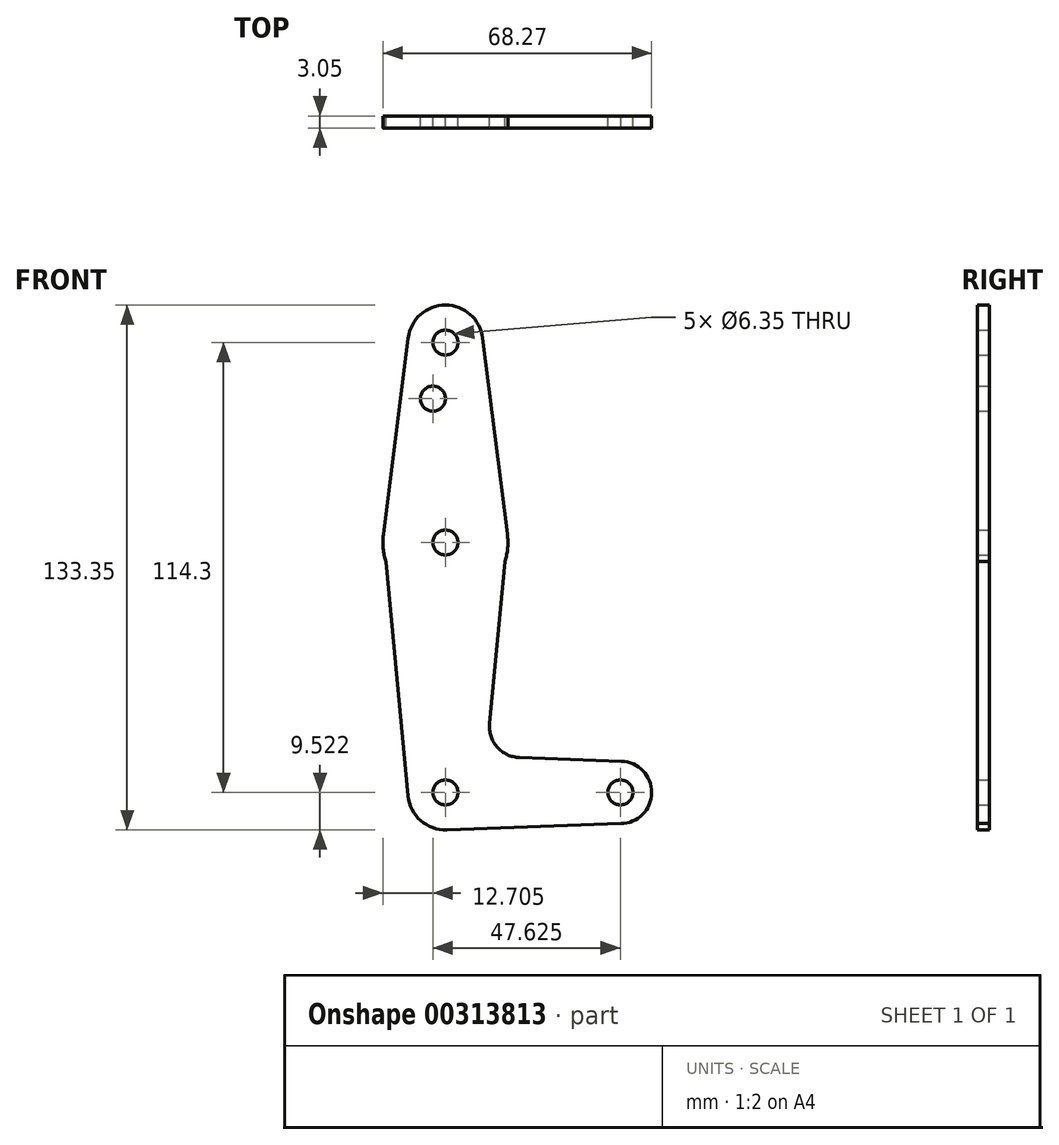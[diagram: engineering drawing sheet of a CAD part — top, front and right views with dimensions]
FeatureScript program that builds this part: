
annotation { "Feature Type Name" : "Feature", "Feature Type Description" : "" }
export const myFeature = defineFeature(function(context is Context, id is Id, definition is map)
    precondition{}
    {
        {
            var Q0;
            Q0=qCreatedBy(makeId("Front.planeOp"),FACE);
            var sketch = newSketch(context, id + "F0", { "sketchPlane" : qUnion([Q0])});
            skCircle(sketch, "E0", {"center": v(0, 72.35) * mm, "radius": 9.53 * mm});
            skCircle(sketch, "E1", {"center": v(0, 72.35) * mm, "radius": 3.18 * mm});
            skLineSegment(sketch, "E2", {"start": v(0, 72.35) * mm, "end": v(0, 21.55) * mm});
            skCircle(sketch, "E3", {"center": v(0, 21.55) * mm, "radius": 15.88 * mm});
            skCircle(sketch, "E4", {"center": v(0, -41.95) * mm, "radius": 9.53 * mm});
            skLineSegment(sketch, "E5", {"start": v(0, -41.95) * mm, "end": v(44.45, -41.95) * mm});
            skCircle(sketch, "E6", {"center": v(44.45, -41.95) * mm, "radius": 7.94 * mm});
            skLineSegment(sketch, "E7", {"start": v(-9.45, 73.54) * mm, "end": v(-15.75, 23.54) * mm});
            skLineSegment(sketch, "E8", {"start": v(-15.75, 23.54) * mm, "end": v(-9.48, -42.84) * mm});
            skLineSegment(sketch, "E9", {"start": v(15.77, 23.4) * mm, "end": v(9.45, 73.54) * mm});
            skLineSegment(sketch, "E10", {"start": v(18.83, -33.1) * mm, "end": v(44.73, -34.02) * mm});
            skLineSegment(sketch, "E11", {"start": v(44.54, -49.88) * mm, "end": v(0, -51.48) * mm});
            skLineSegment(sketch, "E12", {"start": v(11.2, -24.4) * mm, "end": v(15.77, 23.4) * mm});
            skCircle(sketch, "E13", {"center": v(0, 21.55) * mm, "radius": 3.18 * mm});
            skCircle(sketch, "E14", {"center": v(44.45, -41.95) * mm, "radius": 3.18 * mm});
            skCircle(sketch, "E15", {"center": v(0, -41.95) * mm, "radius": 3.18 * mm});
            skLineSegment(sketch, "E16", {"start": v(0, 21.55) * mm, "end": v(0, 58.08) * mm, "construction": true});
            skCircle(sketch, "E17", {"center": v(-3.17, 58.08) * mm, "radius": 3.18 * mm});
            skPoint(sketch, "E18.newPointA", {"position": v(0, -32.42) * mm});
            skArc(sketch, "E18.filletArc", {"start": v(11.2, -24.4) * mm, "mid": v(13.14, -30.4) * mm, "end": v(18.83, -33.1) * mm});
            skSolve(sketch);
        }
        {
            var Q0;
            Q0 = qSketchRegion(id + "F0", true);
            extrude(context, id + "F1", {"entities" : qUnion([Q0]), "depth" : 3.05 * mm});
        }
    });
